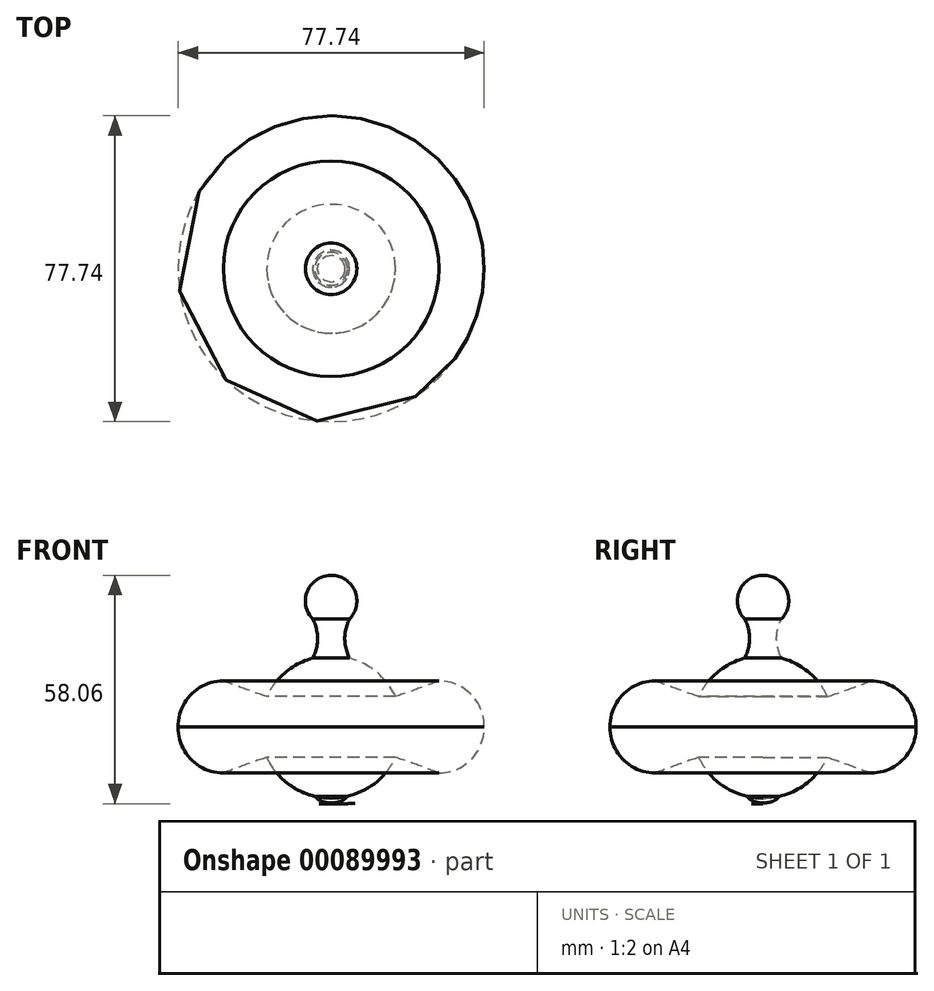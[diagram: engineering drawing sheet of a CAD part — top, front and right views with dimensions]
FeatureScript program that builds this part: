
annotation { "Feature Type Name" : "Feature", "Feature Type Description" : "" }
export const myFeature = defineFeature(function(context is Context, id is Id, definition is map)
    precondition{}
    {
        {
            var Q0;
            Q0=qCreatedBy(makeId("Front.planeOp"),FACE);
            var sketch = newSketch(context, id + "F0", { "sketchPlane" : qUnion([Q0])});
            skLineSegment(sketch, "E0", {"start": v(38.87, 0) * mm, "end": v(38.87, 0) * mm});
            skArc(sketch, "E1", {"start": v(-27.38, 11.7) * mm, "mid": v(-35.58, 8.26) * mm, "end": v(-38.87, 0) * mm});
            skArc(sketch, "E2.MirrorCS", {"start": v(-27.38, -11.7) * mm, "mid": v(-35.58, -8.26) * mm, "end": v(-38.87, 0) * mm});
            skArc(sketch, "E3.MirrorCS", {"start": v(27.38, 11.7) * mm, "mid": v(35.58, 8.26) * mm, "end": v(38.87, 0) * mm});
            skArc(sketch, "E4.MirrorCS", {"start": v(27.38, -11.7) * mm, "mid": v(35.58, -8.26) * mm, "end": v(38.87, 0) * mm});
            skPoint(sketch, "E5.MirrorCS.end.orphan", {"position": v(38.87, 0) * mm});
            skLineSegment(sketch, "E6", {"start": v(-13.7, 11.7) * mm, "end": v(-13.83, 11.7) * mm});
            skLineSegment(sketch, "E7", {"start": v(-16.37, 7.76) * mm, "end": v(-16.37, 7.76) * mm});
            skLineSegment(sketch, "E8", {"start": v(-16.37, -7.76) * mm, "end": v(-16.37, -7.76) * mm});
            skArc(sketch, "E9", {"start": v(-4.68, 17.5) * mm, "mid": v(-3.45, 22.49) * mm, "end": v(-4.7, 27.48) * mm});
            skFitSpline(sketch, "E10", {"points": [v(-4.16, -17.63) * mm, v(-2.65, -18.8) * mm, v(0, -19.35) * mm], "startDerivative": vector(2.93, -2.98) * mm, "endDerivative": vector(5.32, -0.57) * mm});
            skFitSpline(sketch, "E11", {"points": [v(-0.97, -19.24) * mm, v(-0.64, -19.55) * mm, v(0, -19.68) * mm, v(0, -19.68) * mm], "startDerivative": vector(0.47, -0.8) * mm, "endDerivative": vector(-0.05, 0.08) * mm});
            skArc(sketch, "E12.MirrorCS", {"start": v(4.68, 17.5) * mm, "mid": v(3.45, 22.49) * mm, "end": v(4.7, 27.48) * mm});
            skFitSpline(sketch, "E13.MirrorCS", {"points": [v(4.16, -17.63) * mm, v(2.65, -18.8) * mm, v(0, -19.35) * mm], "startDerivative": vector(-2.93, -2.98) * mm, "endDerivative": vector(-5.32, -0.57) * mm});
            skFitSpline(sketch, "E14.MirrorCS", {"points": [v(0.97, -19.24) * mm, v(0.64, -19.55) * mm, v(0, -19.68) * mm, v(0, -19.68) * mm], "startDerivative": vector(-0.47, -0.8) * mm, "endDerivative": vector(0.05, 0.08) * mm});
            skPoint(sketch, "E15.orphan", {"position": v(0, 38.55) * mm});
            skPoint(sketch, "E16.start.orphan", {"position": v(0, -24.95) * mm});
            skLineSegment(sketch, "E17.trimOffspring", {"start": v(14.97, 10.2) * mm, "end": v(14.97, 10.2) * mm});
            skLineSegment(sketch, "E18", {"start": v(0, 38.55) * mm, "end": v(0, 18.11) * mm});
            skArc(sketch, "E19", {"start": v(0, 38.55) * mm, "mid": v(-6.53, 32.02) * mm, "end": v(0, 25.49) * mm});
            skArc(sketch, "E20", {"start": v(0, 25.49) * mm, "mid": v(6.53, 32.02) * mm, "end": v(0, 38.55) * mm});
            skLineSegment(sketch, "E21", {"start": v(0, 18.11) * mm, "end": v(0, -19.35) * mm});
            skFitSpline(sketch, "E22", {"points": [v(13.83, 11.7) * mm, v(14.97, 10.2) * mm], "startDerivative": vector(1.15, -1.5) * mm, "endDerivative": vector(1.15, -1.5) * mm, "construction": true});
            skPoint(sketch, "E23.1.internal.orphan", {"position": v(0, 8.83) * mm});
            skPoint(sketch, "E24.MirrorCS.2.internal.orphan", {"position": v(27.38, -11.7) * mm});
            skPoint(sketch, "E24.MirrorCS.start.orphan", {"position": v(-27.38, -11.7) * mm});
            skFitSpline(sketch, "E25", {"points": [v(-27.38, 11.7) * mm, v(0, 4.8) * mm, v(27.38, 11.7) * mm], "startDerivative": vector(54.76, -20.72) * mm, "endDerivative": vector(54.76, 20.72) * mm});
            skFitSpline(sketch, "E26.MirrorCS", {"points": [v(-27.38, -11.7) * mm, v(0, -4.8) * mm, v(27.38, -11.7) * mm], "startDerivative": vector(54.76, 20.72) * mm, "endDerivative": vector(54.76, -20.72) * mm});
            skPoint(sketch, "E27.start.orphan", {"position": v(0, 11.7) * mm});
            skArc(sketch, "E28", {"start": v(14.97, 10.2) * mm, "mid": v(14.42, 10.96) * mm, "end": v(13.83, 11.7) * mm, "construction": true});
            skArc(sketch, "E29.trimOffspring", {"start": v(-4.16, -17.63) * mm, "mid": v(0, -18.11) * mm, "end": v(4.16, -17.63) * mm});
            skArc(sketch, "E30", {"start": v(-4.68, 17.5) * mm, "mid": v(-11.6, 13.91) * mm, "end": v(-16.37, 7.76) * mm});
            skArc(sketch, "E31", {"start": v(-16.37, -7.76) * mm, "mid": v(0, -18.11) * mm, "end": v(16.37, -7.76) * mm});
            skArc(sketch, "E32", {"start": v(16.37, 7.76) * mm, "mid": v(11.6, 13.91) * mm, "end": v(4.68, 17.5) * mm});
            skArc(sketch, "E33", {"start": v(16.37, -7.76) * mm, "mid": v(18.11, 0) * mm, "end": v(16.37, 7.76) * mm, "construction": true});
            skArc(sketch, "E34.MirrorCS", {"start": v(-16.37, -7.76) * mm, "mid": v(-18.11, 0) * mm, "end": v(-16.37, 7.76) * mm, "construction": true});
            skLineSegment(sketch, "E35.trimOffspring", {"start": v(0, -19.68) * mm, "end": v(0, -19.68) * mm});
            skSolve(sketch);
        }
        {
            var Q0;
            {var subQ1=sQuery(id+"F0.wireOp",EDGE,"E1");Q0=makeQuery(id+"F0.imprint","IMPRINT",FACE,{"disambiguationData":[TD([[makeQuery(id+"F0.imprint","IMPRINT",EDGE,{"derivedFrom":subQ1}),1.0]])]});}
            var Q1;
            {var subQ1=sQuery(id+"F0.wireOp",EDGE,"E9");Q1=makeQuery(id+"F0.imprint","IMPRINT",FACE,{"disambiguationData":[TD([[makeQuery(id+"F0.imprint","IMPRINT",EDGE,{"derivedFrom":subQ1}),-1.0]])]});}
            var Q2;
            {var subQ1=sQuery(id+"F0.wireOp",EDGE,"E19");var subQ5=makeQuery(id+"F0.imprint","INTERSECT",VERTEX,{"derivedFrom":[sQuery(id+"F0.wireOp",EDGE,"E9"),subQ1]});Q2=makeQuery(id+"F0.imprint","IMPRINT",FACE,{"disambiguationData":[TD([[makeQuery(id+"F0.imprint","IMPRINT",EDGE,{"disambiguationData":[TD([[subQ5,1.0]])],"derivedFrom":subQ1}),1.0]])]});}
            var Q3;
            {var subQ0=sQuery(id+"F0.wireOp",EDGE,"E26.MirrorCS");var subQ1=sQuery(id+"F0.wireOp",EDGE,"E21");var subQ2=makeQuery(id+"F0.imprint","INTERSECT",VERTEX,{"derivedFrom":[subQ1,subQ0]});Q3=makeQuery(id+"F0.imprint","IMPRINT",FACE,{"disambiguationData":[TD([[makeQuery(id+"F0.imprint","IMPRINT",EDGE,{"disambiguationData":[TD([[subQ2,-1.0]])],"derivedFrom":subQ1}),-1.0]])]});}
            var Q4;
            {var subQ0=sQuery(id+"F0.wireOp",EDGE,"E31");var subQ1=sQuery(id+"F0.wireOp",EDGE,"E13.MirrorCS");var subQ2=makeQuery(id+"F0.imprint","INTERSECT",VERTEX,{"derivedFrom":[subQ1,subQ0]});Q4=makeQuery(id+"F0.imprint","IMPRINT",FACE,{"disambiguationData":[TD([[makeQuery(id+"F0.imprint","IMPRINT",EDGE,{"disambiguationData":[TD([[subQ2,-1.0]])],"derivedFrom":subQ1}),-1.0]])]});}
            var Q5;
            Q5=sQuery(id+"F0.wireOp",EDGE,"E21");
            revolve(context, id + "F1", {"entities" : qUnion([Q0, Q1, Q2, Q3, Q4]), "axis" : qUnion([Q5]), "revolveType" : RevolveType.FULL});
        }
    });
